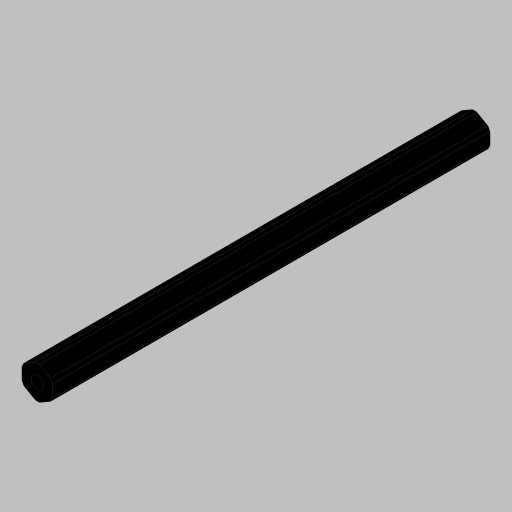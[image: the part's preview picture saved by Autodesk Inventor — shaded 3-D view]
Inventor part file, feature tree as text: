
AUTODESK INVENTOR PART (.ipt)
format: ipt  version: 2023.4 (Build 274418000, 418)  size: 120,320 bytes
history: native  units: in
note: dims shown in document units (in); Inventor stores cm internally (conversion verified against a paired STEP export)
features: extrude x2, projected_geometry x2, hole x1
ambient origin geometry x8: Origin, YZ Plane, XZ Plane, XY Plane, X Axis, Y Axis, Z Axis, Center Point
bodies: Solid1 (feature_tree)
feature tree (5):
  extrude  "Extrusion1"  TaperAngle=0.0deg  [1 undecoded]
  hole  "Hole1"  [1 undecoded]
  extrude  "Extrusion3"  TaperAngle=0.0deg  [1 undecoded]
  projected_geometry  "Project Cut Edges1"
  projected_geometry  "Project Cut Edges2"
note: 3 required parameter values undecoded (feature->parameter linkage not recoverable at this tier; creation-order binding heuristic only, values carry confidence <= 0.55)
